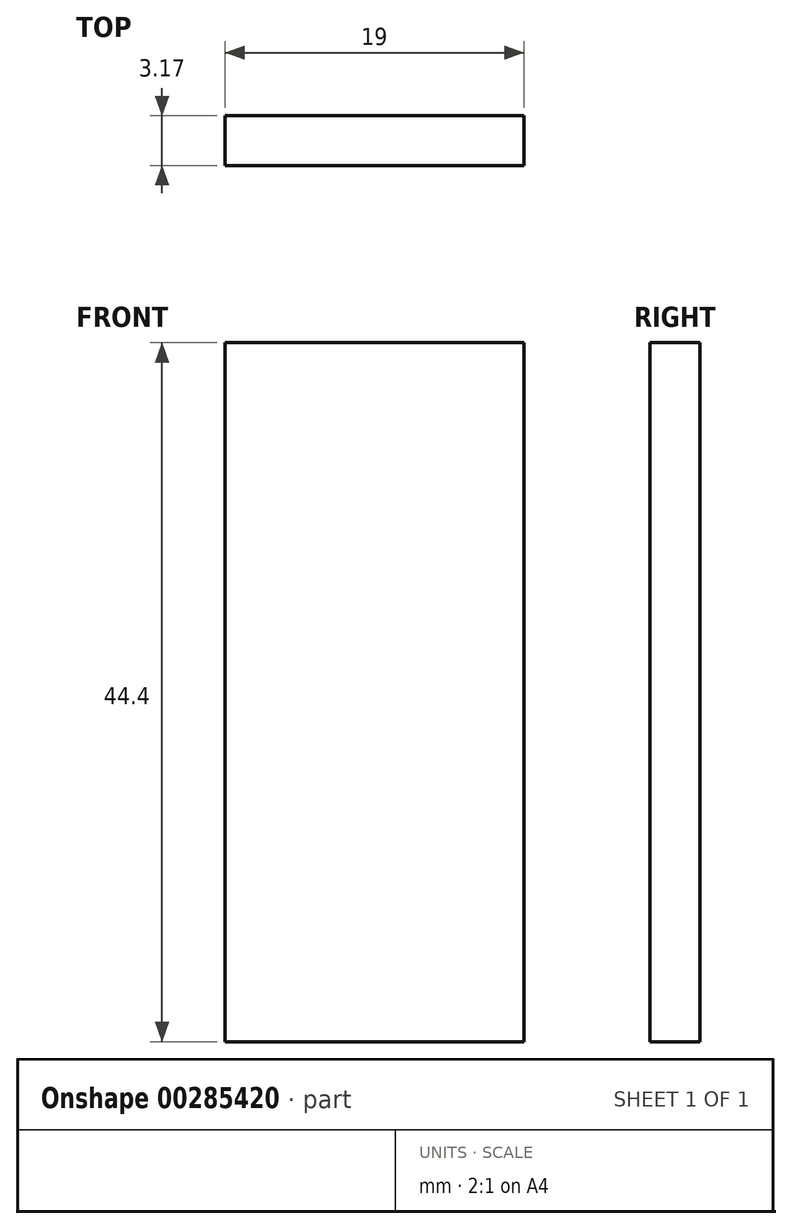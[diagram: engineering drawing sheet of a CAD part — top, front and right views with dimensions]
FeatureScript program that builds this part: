
annotation { "Feature Type Name" : "Feature", "Feature Type Description" : "" }
export const myFeature = defineFeature(function(context is Context, id is Id, definition is map)
    precondition{}
    {
        {
            var Q0;
            Q0=qCreatedBy(makeId("Front.planeOp"),FACE);
            var sketch = newSketch(context, id + "F0", { "sketchPlane" : qUnion([Q0])});
            skLineSegment(sketch, "E0.bottom", {"start": v(0, 0) * mm, "end": v(19, 0) * mm});
            skLineSegment(sketch, "E0.top", {"start": v(0, 44.4) * mm, "end": v(19, 44.4) * mm});
            skLineSegment(sketch, "E0.left", {"start": v(0, 0) * mm, "end": v(0, 44.4) * mm});
            skLineSegment(sketch, "E0.right", {"start": v(19, 0) * mm, "end": v(19, 44.4) * mm});
            skSolve(sketch);
        }
        {
            var Q0;
            Q0 = qSketchRegion(id + "F0", true);
            extrude(context, id + "F1", {"entities" : qUnion([Q0]), "depth" : 3.17 * mm, "offsetDistance" : 25 * mm});
        }
    });
